# Revit family: Edelstahlrohrschelle V4A, M12, Ø102-168, Gummi
name_source: partatom
category: HLS-Bauteile
revit_build: Autodesk Revit 2017 (Build: 20190507_1515(x64)
units: mm (PartAtom-declared; Revit-internal decimal feet)

## family parameters
Arbeitsebenenbasiert = Ja
Beim Laden mit Abzugskörper schneiden = Nein
Bemaßung runder Anschluss = Durchmesser verwenden
Gemeinsam genutzt = Ja
Immer vertikal = Nein
Raumberechnungspunkt = Nein
Teiletyp = Normal

## types (9) — shared parameters
A = 20 mm  [stored 0.0656168 ft]
Anschluss = M12
Anschlußhöhe = 20 mm
Bauart = zweiteilig
Baustoffklasse = B2
DF1 = 21 mm  [stored 0.0688976 ft]
DF2 = 25 mm  [stored 0.082021 ft]
DS = 6 mm  [stored 0.019685 ft]
DVS = 9 mm  [stored 0.0295276 ft]
Dämmstärke = 6 mm  [stored 0.019685 ft]
Fabrikat = MEFA
Farbe Schalldämmeinlage = schwarz
Firma = MEFA Befestigungs- und Montagesysteme GmbH
HGA = 11 mm  [stored 0.0360892 ft]
Kurztext1 = Rohrschelle Edelstahl V4A 25x3,0
MB = 25 mm  [stored 0.082021 ft]
MD = 3 mm  [stored 0.00984252 ft]
Material = Edelstahl
Material Schalldämmeinlage = TPE
Materialmaße = 25x3,0 mm
Mengeneinheit = St
Schalldämmeinlage = Gummi
Verschluss = Schraubenverschluss
Verschluss-Schraube = M8
Vorgabe-Ansicht = 1219 mm
max. Temperaturbeständigkeit = 100 °C
max. zul. Last horizontal = 0.00 kN
max. zul. Last vertikal = 0.00 kN
vpe = 50 St
zero-valued in all types: Nennweite DN Rohr, Rohraußendurchmesser, Stärke Material

## per-type parameters (varying)
| type | AB | Achsabstand | Artikelnummer | B | D | D0 | Dmax | Dmin | EAN | Gewicht | Gewicht pro Bauteil | H | Kurztext2 | R | RM | Rohraußendurchmesser Zoll | S | max. Rohraußendurchmesser | min. Rohraußendurchmesser |
| Edelstahlrohrschelle V4A, M12, Ø102-107, Gummi | 5 mm  [stored 0.0164042 ft] | 150 mm | 0490317 | 171 mm | 107 mm  [stored 0.35105 ft] | 119 mm  [stored 0.39042 ft] | 107 mm  [stored 0.35105 ft] | 102 mm | 4250928413161 | 0.37 kg | 0.37 kg | 136 mm | 102 - 107 mm M12 TPE | 60 mm | 63 mm | Zoll | 150 mm | 107 mm  [stored 0.35105 ft] | 102 mm |
| Edelstahlrohrschelle V4A, M12, Ø108-116, Gummi | 8 mm  [stored 0.0262467 ft] | 158 mm | 0490318 | 180 mm | 116 mm  [stored 0.380577 ft] | 128 mm  [stored 0.419948 ft] | 116 mm  [stored 0.380577 ft] | 108 mm  [stored 0.354331 ft] | 4250928413178 | 0.38 kg | 0.38 kg | 145 mm | 108 - 116 mm M12 TPE | 64 mm  [stored 0.209974 ft] | 67 mm | 4 Zoll | 159 mm | 116 mm  [stored 0.380577 ft] | 108 mm  [stored 0.354331 ft] |
| Edelstahlrohrschelle V4A, M12, Ø119-127, Gummi | 8 mm  [stored 0.0262467 ft] | 169 mm | 0496319 | 191 mm | 127 mm | 139 mm  [stored 0.456037 ft] | 127 mm | 119 mm  [stored 0.39042 ft] | 4250928413451 | 0.41 kg | 0.41 kg | 156 mm | 119 - 127 mm M12 TPE | 70 mm | 73 mm | Zoll | 170 mm | 127 mm | 119 mm  [stored 0.39042 ft] |
| Edelstahlrohrschelle V4A, M12, Ø128-132, Gummi | 4 mm  [stored 0.0131234 ft] | 176 mm | 0496320 | 196 mm | 132 mm  [stored 0.433071 ft] | 144 mm | 132 mm  [stored 0.433071 ft] | 128 mm  [stored 0.419948 ft] | 4250928413468 | 0.43 kg | 0.43 kg | 161 mm | 128 - 132 mm M12 TPE | 72 mm  [stored 0.23622 ft] | 75 mm | Zoll | 175 mm | 132 mm  [stored 0.433071 ft] | 128 mm  [stored 0.419948 ft] |
| Edelstahlrohrschelle V4A, M12, Ø133-141, Gummi | 8 mm  [stored 0.0262467 ft] | 184 mm | 0496321 | 205 mm | 141 mm | 153 mm | 141 mm | 133 mm  [stored 0.436352 ft] | 4250928413475 | 0.44 kg | 0.44 kg | 170 mm | 133 - 141 mm M12 TPE | 77 mm | 80 mm | 5 Zoll | 184 mm | 141 mm | 133 mm  [stored 0.436352 ft] |
| Edelstahlrohrschelle V4A, M12, Ø142-149, Gummi | 7 mm  [stored 0.0229659 ft] | 192 mm | 0496322 | 213 mm | 149 mm | 161 mm | 149 mm | 142 mm | 4250928413482 | 0.46 kg | 0.46 kg | 178 mm | 142 - 149 mm M12 TPE | 81 mm | 84 mm | Zoll | 192 mm | 149 mm | 142 mm |
| Edelstahlrohrschelle V4A, M12, Ø150-158, Gummi | 8 mm  [stored 0.0262467 ft] | 201 mm | 0496323 | 222 mm | 158 mm | 170 mm | 158 mm | 150 mm | 4250928413499 | 0.48 kg | 0.48 kg | 187 mm | 150 - 158 mm M12 TPE | 85 mm  [stored 0.278871 ft] | 88 mm | Zoll | 201 mm | 158 mm | 150 mm |
| Edelstahlrohrschelle V4A, M12, Ø159-163, Gummi | 4 mm  [stored 0.0131234 ft] | 207 mm | 0496324 | 227 mm | 163 mm | 175 mm | 163 mm | 159 mm | 4250928413505 | 0.50 kg | 0.50 kg | 192 mm | 159 - 163 mm M12 TPE | 88 mm | 91 mm | Zoll | 206 mm | 163 mm | 159 mm |
| Edelstahlrohrschelle V4A, M12, Ø164-168, Gummi | 4 mm  [stored 0.0131234 ft] | 212 mm | 0496325 | 232 mm | 168 mm | 180 mm | 168 mm | 164 mm | 4250928413512 | 0.50 kg | 0.50 kg | 197 mm | 164 - 168 mm M12 TPE | 90 mm | 93 mm  [stored 0.305118 ft] | 6 Zoll | 211 mm | 168 mm | 164 mm |

note: [stored X ft] marks values corroborated as IEEE doubles in the binary element streams (Revit-internal decimal feet)

## geometry (parser evidence)
native form markers: Sweep x4
no freeform markers — native parametric forms only
